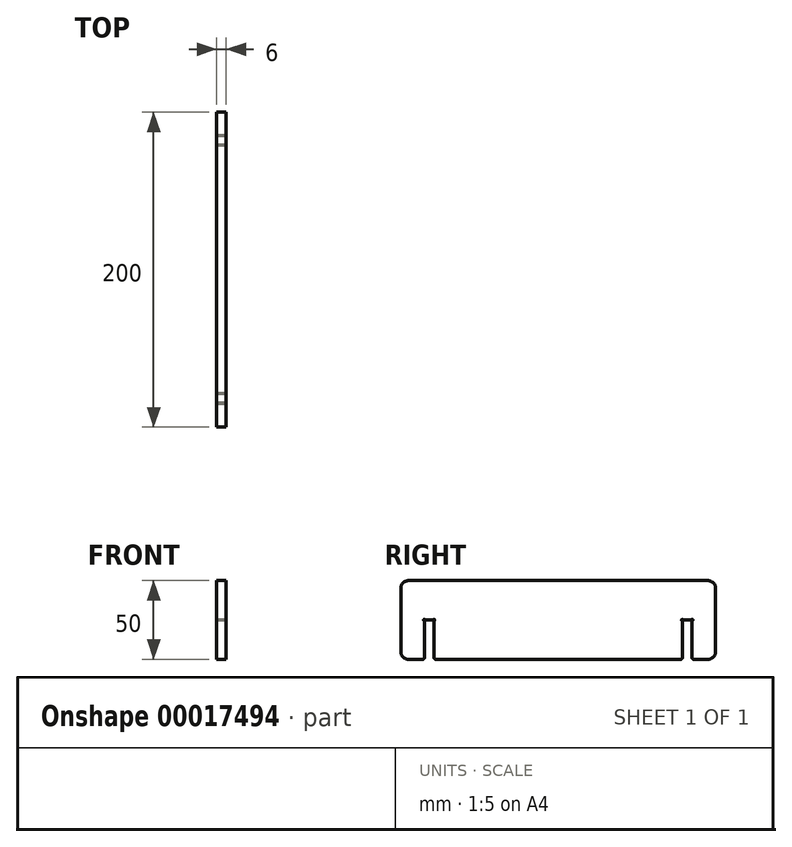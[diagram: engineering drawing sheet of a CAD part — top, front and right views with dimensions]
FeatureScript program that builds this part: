
annotation { "Feature Type Name" : "Feature", "Feature Type Description" : "" }
export const myFeature = defineFeature(function(context is Context, id is Id, definition is map)
    precondition{}
    {
        {
            var Q0;
            Q0=qCreatedBy(makeId("Right.planeOp"),FACE);
            var sketch = newSketch(context, id + "F0", { "sketchPlane" : qUnion([Q0])});
            skLineSegment(sketch, "E0.bottom", {"start": v(-95, 0) * mm, "end": v(-86, 0) * mm});
            skLineSegment(sketch, "E0.top", {"start": v(-95, 50) * mm, "end": v(95, 50) * mm});
            skLineSegment(sketch, "E0.left", {"start": v(-100, 5) * mm, "end": v(-100, 45) * mm});
            skLineSegment(sketch, "E0.right", {"start": v(100, 5) * mm, "end": v(100, 45) * mm});
            skLineSegment(sketch, "E1", {"start": v(0, 0) * mm, "end": v(0, 107.33) * mm, "construction": true});
            skLineSegment(sketch, "E2.top", {"start": v(-84.5, 25) * mm, "end": v(-79.4, 25) * mm});
            skLineSegment(sketch, "E2.left", {"start": v(-85, 1) * mm, "end": v(-85, 24.5) * mm});
            skLineSegment(sketch, "E2.right", {"start": v(-78.9, 1) * mm, "end": v(-78.9, 24.5) * mm});
            skLineSegment(sketch, "E3.top", {"start": v(84.5, 25) * mm, "end": v(79.4, 25) * mm});
            skLineSegment(sketch, "E3.left", {"start": v(85, 1) * mm, "end": v(85, 24.5) * mm});
            skLineSegment(sketch, "E3.right", {"start": v(78.9, 1) * mm, "end": v(78.9, 24.5) * mm});
            skLineSegment(sketch, "E4.trimOffspring", {"start": v(-77.9, 0) * mm, "end": v(77.9, 0) * mm});
            skLineSegment(sketch, "E5.trimOffspring", {"start": v(86, 0) * mm, "end": v(95, 0) * mm});
            skArc(sketch, "E6", {"start": v(-84.5, 25) * mm, "mid": v(-85.35, 25.35) * mm, "end": v(-85, 24.5) * mm});
            skArc(sketch, "E7", {"start": v(-78.9, 24.5) * mm, "mid": v(-78.55, 25.35) * mm, "end": v(-79.4, 25) * mm});
            skArc(sketch, "E8", {"start": v(79.4, 25) * mm, "mid": v(78.55, 25.35) * mm, "end": v(78.9, 24.5) * mm});
            skArc(sketch, "E9", {"start": v(85, 24.5) * mm, "mid": v(85.35, 25.35) * mm, "end": v(84.5, 25) * mm});
            skPoint(sketch, "E10.visualSharp", {"position": v(-100, 50) * mm});
            skArc(sketch, "E10.filletArc", {"start": v(-95, 50) * mm, "mid": v(-98.54, 48.54) * mm, "end": v(-100, 45) * mm});
            skPoint(sketch, "E11.visualSharp", {"position": v(-100, 0) * mm});
            skArc(sketch, "E11.filletArc", {"start": v(-100, 5) * mm, "mid": v(-98.54, 1.46) * mm, "end": v(-95, 0) * mm});
            skPoint(sketch, "E12.visualSharp", {"position": v(100, 50) * mm});
            skArc(sketch, "E12.filletArc", {"start": v(100, 45) * mm, "mid": v(98.54, 48.54) * mm, "end": v(95, 50) * mm});
            skPoint(sketch, "E13.visualSharp", {"position": v(100, 0) * mm});
            skArc(sketch, "E13.filletArc", {"start": v(95, 0) * mm, "mid": v(98.54, 1.46) * mm, "end": v(100, 5) * mm});
            skPoint(sketch, "E14.visualSharp", {"position": v(78.9, 0) * mm});
            skArc(sketch, "E14.filletArc", {"start": v(77.9, 0) * mm, "mid": v(78.6, 0.3) * mm, "end": v(78.9, 1) * mm});
            skPoint(sketch, "E15.visualSharp", {"position": v(85, 0) * mm});
            skArc(sketch, "E15.filletArc", {"start": v(85, 1) * mm, "mid": v(85.3, 0.3) * mm, "end": v(86, 0) * mm});
            skPoint(sketch, "E16.visualSharp", {"position": v(-85, 0) * mm});
            skArc(sketch, "E16.filletArc", {"start": v(-86, 0) * mm, "mid": v(-85.3, 0.3) * mm, "end": v(-85, 1) * mm});
            skPoint(sketch, "E17.visualSharp", {"position": v(-78.9, 0) * mm});
            skArc(sketch, "E17.filletArc", {"start": v(-78.9, 1) * mm, "mid": v(-78.6, 0.3) * mm, "end": v(-77.9, 0) * mm});
            skSolve(sketch);
        }
        {
            var Q0;
            Q0 = qSketchRegion(id + "F0", true);
            extrude(context, id + "F1", {"entities" : qUnion([Q0]), "depth" : 6 * mm});
        }
    });
